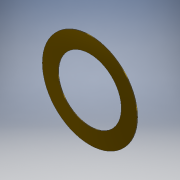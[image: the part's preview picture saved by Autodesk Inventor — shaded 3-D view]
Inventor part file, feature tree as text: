
AUTODESK INVENTOR PART (.ipt)
format: ipt  version: 2018 (Build 220112000, 112)  size: 113,664 bytes
history: native  units: mm
features: extrude x1, sketch x1
ambient origin geometry x8: Origin, YZ Plane, XZ Plane, XY Plane, X Axis, Y Axis, Z Axis, Center Point
bodies: Solid1 (feature_tree)
feature tree (2):
  extrude  "Extrusion1"  Depth=0.01mm
  sketch  "Sketch1"  dims[d0=1.0mm d1=1.5mm d2=0.01mm d3=0.0mm]
